# Revit family: ledspot3c-c-p_37w-ble2-3000-36d-bl_541001167300
name_source: partatom
category: Leuchten
revit_build: Autodesk Revit 2016 (Build: 20190508_0715(x64)
units: mm (PartAtom-declared; Revit-internal decimal feet)

## family parameters
Basisbauteil = Fläche
Beim Laden mit Abzugskörper schneiden = Nein
Bemaßung runder Anschluss = Durchmesser verwenden
Gemeinsam genutzt = Nein
Lichtquelle = Nein
Raumberechnungspunkt = Nein
Teiletyp = Normal

## types (1)
- LEDSpot3C-C-P 37W-BLE2-3000-36D-BL (1 x LED, 2960 lm, 3000)
    Approval mark = CE, ENEC
    Beschreibung = High performance compact track spot with high luminous efficiency and homogeneous light distribution. Various beam angles achievable with exchangeable reflectors. Fitting common Global/Nordic Aluminum® 3C Tracks – and many other standard types. Low glare
    CIE Flux Codes = 92 99 100 99 100
    Color Rendering = 90
    Color Temperature = 3000
    Control Gear = Electronic ballast
    Frequency = 60 Hz
    Height = 246 mm
    Hersteller = OPPLE
    Lamp Light Flux = 2960 lm
    Lamp count = 1
    Lampe = 1 x LED
    Length = 299 mm
    Luminous efficacy = 80 lm/W
    ModVariant = Nein
    Modell = 541001167300
    Mounting Place = Ceiling, Pole
    Mounting Type = Rail mounted
    Number of Poles = 1
    OnlyDefault = Ja
    Power Factor = 1
    Product Name = LEDSpot3C-C-P 37W-BLE2-3000-36D-BL
    Product group = Track mounted spotlight
    ProductGroupID = 12
    Protection Class = Protection class II
    Protection Degree = IP 20
    RLX_Detail_Level = 1
    RlxData = <blob elided: 106389 chars, md5=75a4b785>
    Scheinlast = 37 VA
    Socket = socket
    Standby Power = 0 W
    System Light Flux = 2960 lm
    System Power = 37 W
    Typenbild = web_pf_3cc_37w_bl.jpg
    Typenkommentare = Product without accessories
    URL = http://relux.com
    VarID = ---
    Voltage = 230 V
    Voltage Range = 220-240 V
    Vorgabe-Ansicht = 1800 mm
    Weight = 0.00 kg
    Width = 85 mm

## geometry (parser evidence)
native form markers: Sweep x13
no freeform markers — native parametric forms only
